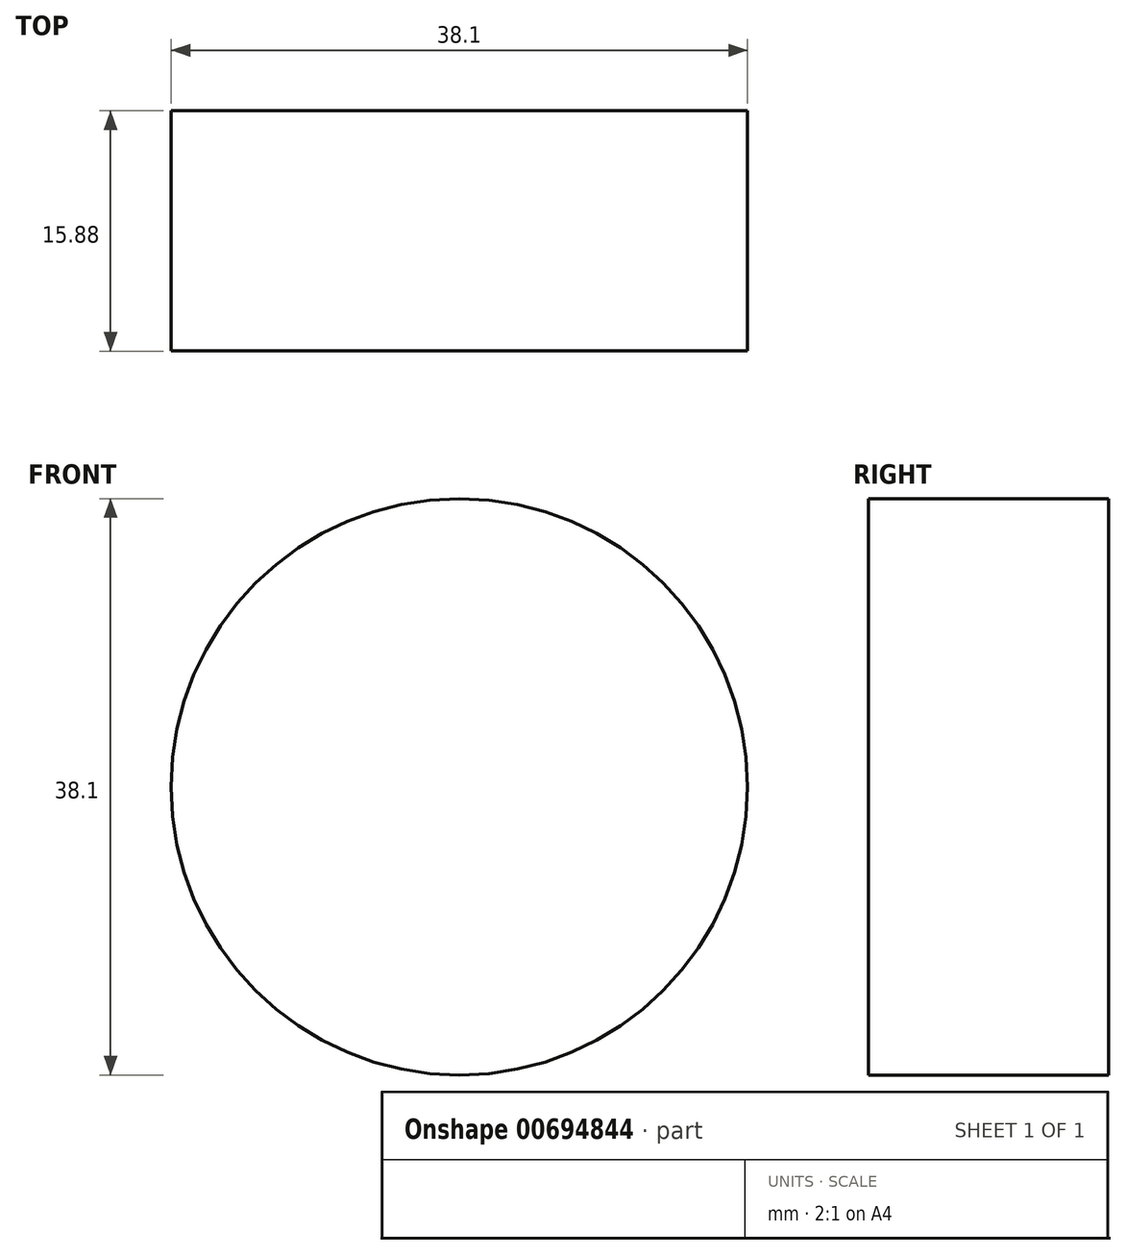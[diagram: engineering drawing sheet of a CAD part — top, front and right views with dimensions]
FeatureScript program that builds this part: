
annotation { "Feature Type Name" : "Feature", "Feature Type Description" : "" }
export const myFeature = defineFeature(function(context is Context, id is Id, definition is map)
    precondition{}
    {
        {
            var Q0;
            Q0=qCreatedBy(makeId("Front.planeOp"),FACE);
            var sketch = newSketch(context, id + "F0", { "sketchPlane" : qUnion([Q0])});
            skCircle(sketch, "E0", {"center": v(0, 0) * mm, "radius": 19.05 * mm});
            skSolve(sketch);
        }
        {
            var Q0;
            Q0 = qSketchRegion(id + "F0", true);
            extrude(context, id + "F1", {"entities" : qUnion([Q0]), "depth" : 15.88 * mm, "offsetDistance" : 25.4 * mm});
        }
        {
            var Q0;
            Q0=qCreatedBy(makeId("Front.planeOp"),FACE);
            var sketch = newSketch(context, id + "F2", { "sketchPlane" : qUnion([Q0])});
            skCircle(sketch, "E1", {"center": v(0, 0) * mm, "radius": 9.52 * mm});
            skSolve(sketch);
        }
        {
            var Q0;
            Q0 = qSketchRegion(id + "F2", true);
            extrude(context, id + "F3", {"entities" : qUnion([Q0]), "operationType" : NewBodyOperationType.REMOVE, "oppositeDirection" : true, "depth" : 12.7 * mm, "offsetDistance" : 25.4 * mm});
        }
        {
            var Q0;
            Q0 = qSketchRegion(id + "F2", true);
            extrude(context, id + "F4", {"entities" : qUnion([Q0]), "operationType" : NewBodyOperationType.REMOVE, "oppositeDirection" : true, "depth" : 12.7 * mm, "offsetDistance" : 25.4 * mm});
        }
    });
